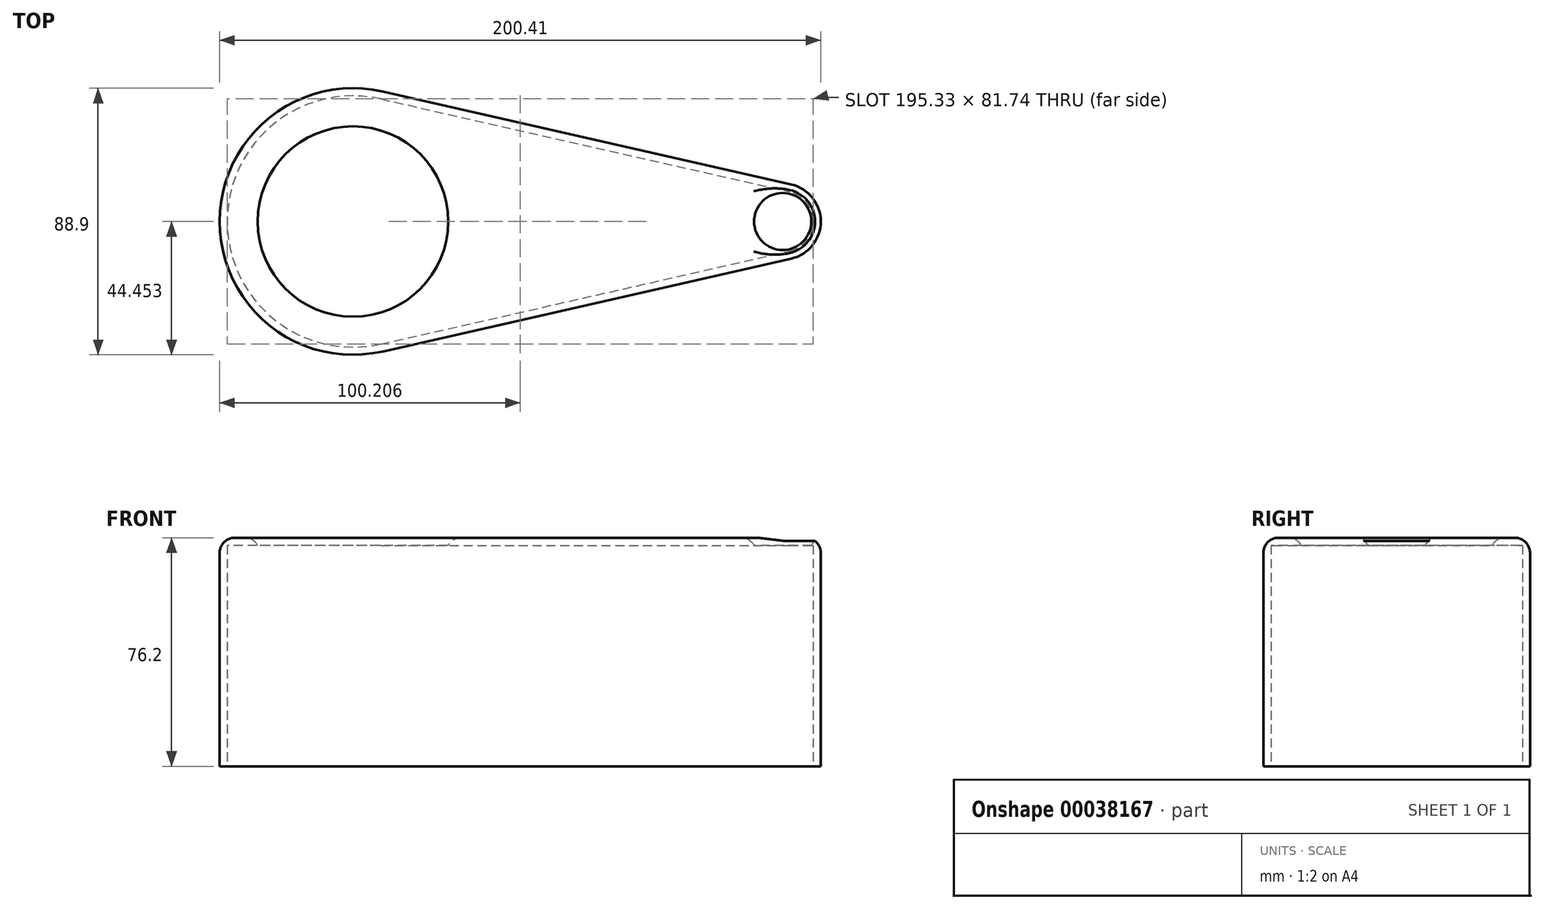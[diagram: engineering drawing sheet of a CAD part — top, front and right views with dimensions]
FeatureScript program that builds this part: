
annotation { "Feature Type Name" : "Feature", "Feature Type Description" : "" }
export const myFeature = defineFeature(function(context is Context, id is Id, definition is map)
    precondition{}
    {
        {
            var Q0;
            Q0=qCreatedBy(makeId("Top.planeOp"),FACE);
            var sketch = newSketch(context, id + "F0", { "sketchPlane" : qUnion([Q0])});
            skCircle(sketch, "E0", {"center": v(-73.19, 38.62) * mm, "radius": 44.45 * mm});
            skCircle(sketch, "E1", {"center": v(70.07, 38.62) * mm, "radius": 12.7 * mm});
            skLineSegment(sketch, "E2", {"start": v(-63.34, 81.97) * mm, "end": v(72.89, 51) * mm});
            skLineSegment(sketch, "E3", {"start": v(-63.34, -4.72) * mm, "end": v(72.89, 26.24) * mm});
            skSolve(sketch);
        }
        {
            var Q0;
            {var subQ0=sQuery(id+"F0.wireOp",EDGE,"E1");var subQ2=makeQuery(id+"F0.imprint","INTERSECT",VERTEX,{"derivedFrom":[subQ0,sQuery(id+"F0.wireOp",EDGE,"E2")]});Q0=makeQuery(id+"F0.imprint","IMPRINT",FACE,{"disambiguationData":[TD([[makeQuery(id+"F0.imprint","IMPRINT",EDGE,{"disambiguationData":[TD([[subQ2,-1.0]])],"derivedFrom":subQ0}),1.0]])]});}
            var Q1;
            {var subQ1=sQuery(id+"F0.wireOp",EDGE,"E2");Q1=makeQuery(id+"F0.imprint","IMPRINT",FACE,{"disambiguationData":[TD([[makeQuery(id+"F0.imprint","IMPRINT",EDGE,{"derivedFrom":subQ1}),-1.0]])]});}
            var Q2;
            {var subQ0=sQuery(id+"F0.wireOp",EDGE,"E0");var subQ2=makeQuery(id+"F0.imprint","INTERSECT",VERTEX,{"derivedFrom":[subQ0,sQuery(id+"F0.wireOp",EDGE,"E2")]});Q2=makeQuery(id+"F0.imprint","IMPRINT",FACE,{"disambiguationData":[TD([[makeQuery(id+"F0.imprint","IMPRINT",EDGE,{"disambiguationData":[TD([[subQ2,-1.0]])],"derivedFrom":subQ0}),1.0]])]});}
            extrude(context, id + "F1", {"entities" : qUnion([Q0, Q1, Q2]), "depth" : 76.2 * mm});
        }
        {
            var Q0;
            Q0=makeQuery(id+"F1.opExtrude","CAP_FACE",FACE,{"disambiguationData":[OSD([sQuery(id+"F0.wireOp",EDGE,"E0"),sQuery(id+"F0.wireOp",EDGE,"E1"),sQuery(id+"F0.wireOp",EDGE,"E2"),sQuery(id+"F0.wireOp",EDGE,"E3")])],"isStart":false});
            var sketch = newSketch(context, id + "F2", { "sketchPlane" : qUnion([Q0])});
            skCircle(sketch, "E4", {"center": v(-73.19, 38.62) * mm, "radius": 31.75 * mm});
            skCircle(sketch, "E5", {"center": v(70.07, 38.62) * mm, "radius": 9.53 * mm});
            skSolve(sketch);
        }
        {
            var Q0;
            Q0=makeQuery(id+"F1.opExtrude","CAP_FACE",FACE,{"disambiguationData":[OSD([sQuery(id+"F0.wireOp",EDGE,"E0"),sQuery(id+"F0.wireOp",EDGE,"E1"),sQuery(id+"F0.wireOp",EDGE,"E2"),sQuery(id+"F0.wireOp",EDGE,"E3")])],"isStart":true});
            shell(context, id + "F3", {"entities" : qUnion([Q0]), "thickness" : 2.54 * mm});
        }
        {
            var Q0;
            Q0=makeQuery(id+"F2.imprint","IMPRINT",FACE,{"disambiguationData":[TD([[makeQuery(id+"F2.imprint","IMPRINT",EDGE,{"derivedFrom":sQuery(id+"F2.wireOp",EDGE,"E4")}),1.0]])]});
            var Q1;
            Q1=makeQuery(id+"F2.imprint","IMPRINT",FACE,{"disambiguationData":[TD([[makeQuery(id+"F2.imprint","IMPRINT",EDGE,{"derivedFrom":sQuery(id+"F2.wireOp",EDGE,"E5")}),1.0]])]});
            extrude(context, id + "F4", {"entities" : qUnion([Q0, Q1]), "operationType" : NewBodyOperationType.REMOVE, "oppositeDirection" : true, "depth" : 63.5 * mm});
        }
        {
            var Q0;
            Q0=makeQuery(id+"F1.opExtrude","CAP_FACE",FACE,{"disambiguationData":[OSD([sQuery(id+"F0.wireOp",EDGE,"E0"),sQuery(id+"F0.wireOp",EDGE,"E1"),sQuery(id+"F0.wireOp",EDGE,"E2"),sQuery(id+"F0.wireOp",EDGE,"E3")])],"isStart":false});
            var Q1;
            Q1=makeQuery(id+"F4.boolean.opBoolean","COPY",FACE,{"derivedFrom":makeQuery(id+"F4.opExtrude","CAP_FACE",FACE,{"disambiguationData":[OSD([sQuery(id+"F2.wireOp",EDGE,"E4")])],"isStart":false})});
            var Q2;
            Q2=makeQuery(id+"F4.boolean.opBoolean","COPY",FACE,{"derivedFrom":makeQuery(id+"F4.opExtrude","CAP_FACE",FACE,{"disambiguationData":[OSD([sQuery(id+"F2.wireOp",EDGE,"E5")])],"isStart":false})});
            fillet(context, id + "F5", {"entities" : qUnion([Q0, Q1, Q2]), "radius" : 5.08 * mm, "tangentPropagation" : true, "allowEdgeOverflow" : false});
        }
    });
